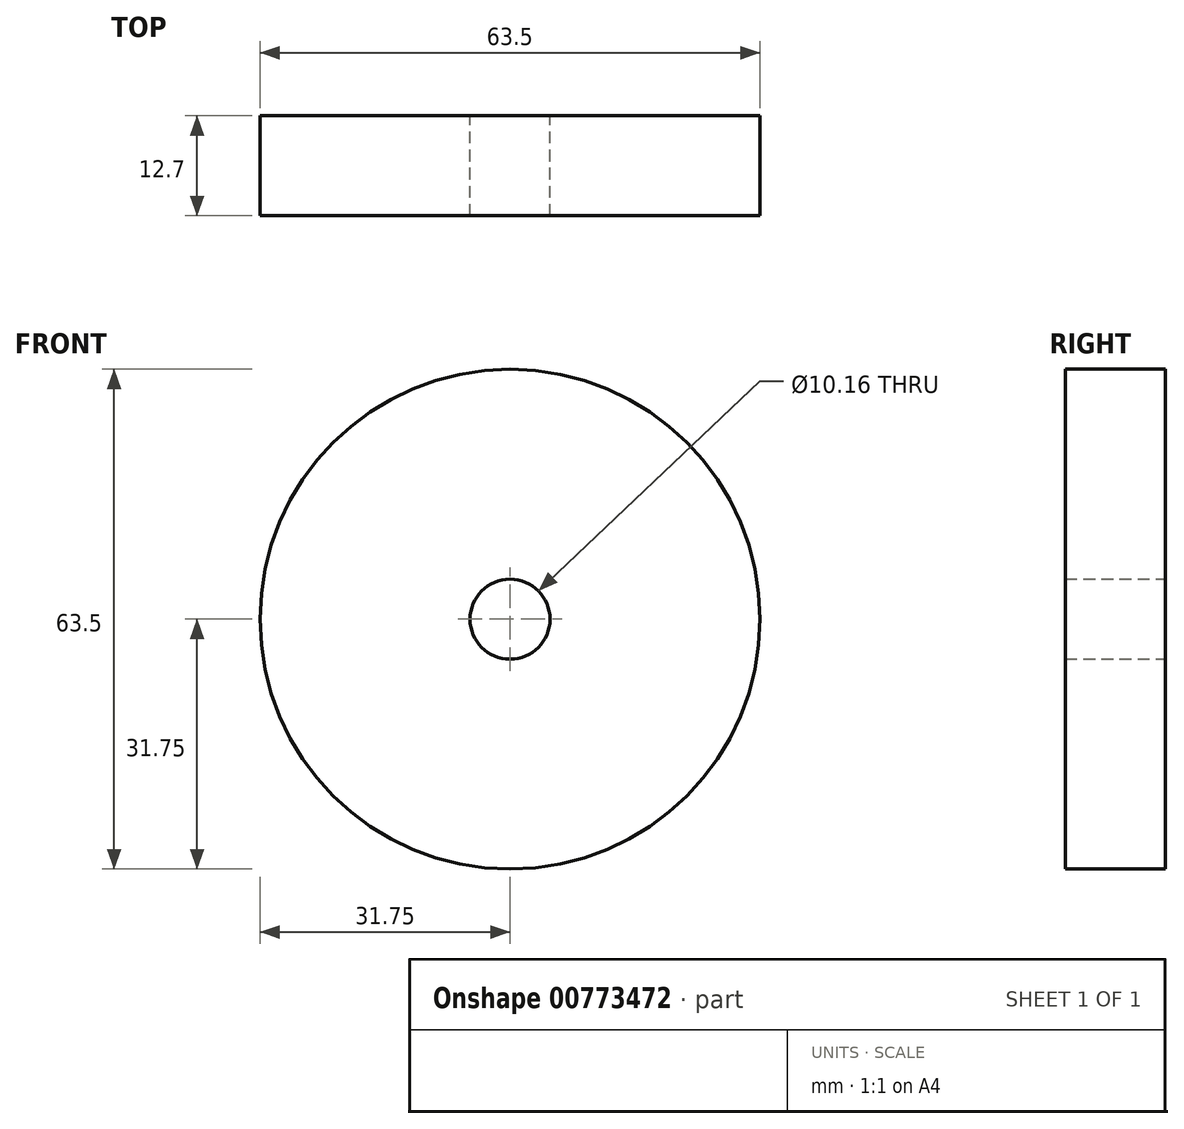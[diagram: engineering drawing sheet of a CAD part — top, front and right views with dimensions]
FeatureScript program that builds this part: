
annotation { "Feature Type Name" : "Feature", "Feature Type Description" : "" }
export const myFeature = defineFeature(function(context is Context, id is Id, definition is map)
    precondition{}
    {
        {
            var Q0;
            Q0=qCreatedBy(makeId("Front.planeOp"),FACE);
            var sketch = newSketch(context, id + "F0", { "sketchPlane" : qUnion([Q0])});
            skCircle(sketch, "E0", {"center": v(0, 0) * mm, "radius": 31.75 * mm});
            skCircle(sketch, "E1", {"center": v(0, 0) * mm, "radius": 5.08 * mm});
            skSolve(sketch);
        }
        {
            var Q0;
            Q0=makeQuery(id+"F0.imprint","IMPRINT",FACE,{"disambiguationData":[TD([[makeQuery(id+"F0.imprint","IMPRINT",EDGE,{"derivedFrom":sQuery(id+"F0.wireOp",EDGE,"E0")}),1.0]])]});
            extrude(context, id + "F1", {"entities" : qUnion([Q0]), "depth" : 12.7 * mm, "offsetDistance" : 25.4 * mm});
        }
    });
